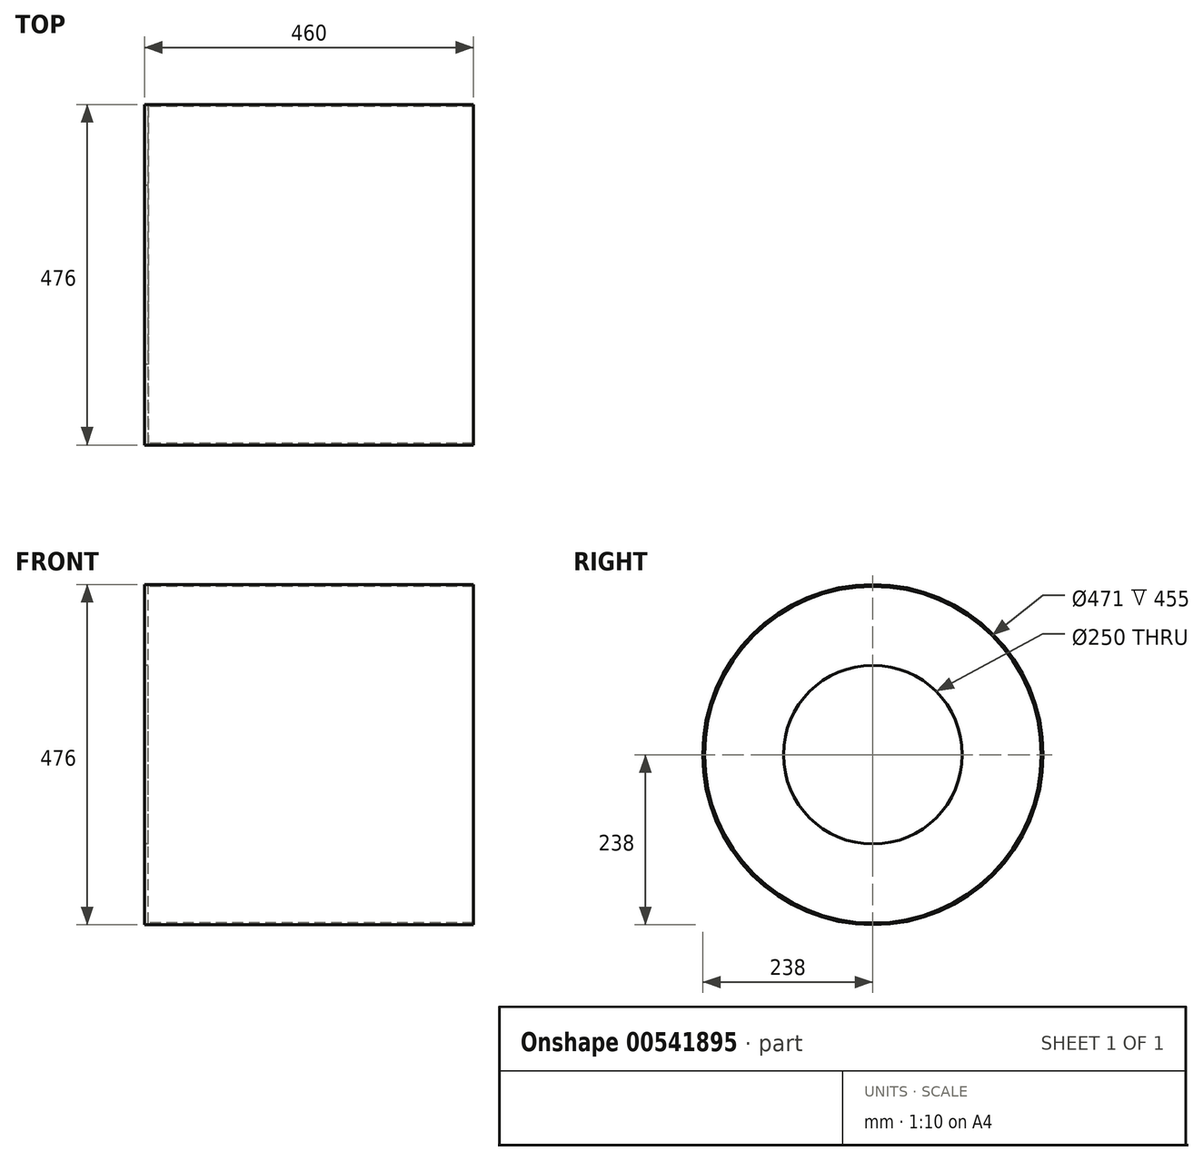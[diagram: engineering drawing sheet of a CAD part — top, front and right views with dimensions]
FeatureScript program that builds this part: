
annotation { "Feature Type Name" : "Feature", "Feature Type Description" : "" }
export const myFeature = defineFeature(function(context is Context, id is Id, definition is map)
    precondition{}
    {
        {
            var Q0;
            Q0=qCreatedBy(makeId("Right.planeOp"),FACE);
            var sketch = newSketch(context, id + "F0", { "sketchPlane" : qUnion([Q0])});
            skCircle(sketch, "E0", {"center": v(0, 0) * mm, "radius": 238 * mm});
            skCircle(sketch, "E1", {"center": v(0, 0) * mm, "radius": 235.5 * mm});
            skSolve(sketch);
        }
        {
            var Q0;
            Q0 = qSketchRegion(id + "F0", true);
            extrude(context, id + "F1", {"entities" : qUnion([Q0]), "depth" : 460 * mm, "offsetDistance" : 25 * mm});
        }
        {
            var Q0;
            Q0=qCreatedBy(makeId("Right.planeOp"),FACE);
            var sketch = newSketch(context, id + "F2", { "sketchPlane" : qUnion([Q0])});
            skCircle(sketch, "E2", {"center": v(0, 0) * mm, "radius": 238 * mm});
            skSolve(sketch);
        }
        {
            var Q0;
            Q0 = qSketchRegion(id + "F2", true);
            extrude(context, id + "F3", {"entities" : qUnion([Q0]), "operationType" : NewBodyOperationType.ADD, "depth" : 5 * mm, "offsetDistance" : 25 * mm});
        }
        {
            var Q0;
            Q0=makeQuery(id+"F3.boolean.opBoolean","MERGE",FACE,{"derivedFrom":[makeQuery(id+"F1.opExtrude","CAP_FACE",FACE,{"disambiguationData":[OSD([sQuery(id+"F0.wireOp",EDGE,"E0"),sQuery(id+"F0.wireOp",EDGE,"E1")])],"isStart":true}),makeQuery(id+"F3.opExtrude","CAP_FACE",FACE,{"disambiguationData":[OSD([sQuery(id+"F2.wireOp",EDGE,"E2")])],"isStart":true})]});
            var sketch = newSketch(context, id + "F4", { "sketchPlane" : qUnion([Q0])});
            skCircle(sketch, "E3", {"center": v(0, 0) * mm, "radius": 125 * mm});
            skSolve(sketch);
        }
        {
            var Q0;
            Q0=sQuery(id+"F4.wireOp",VERTEX,"E3.center");
            var Q1;
            Q1=makeQuery(id+"F1.opExtrude","SWEPT_BODY",BODY,{"disambiguationData":[OSD([sQuery(id+"F0.wireOp",EDGE,"E0"),sQuery(id+"F0.wireOp",EDGE,"E1")])]});
            hole(context, id + "F5", {"style" : HoleStyle.SIMPLE, "endStyle" : HoleEndStyle.BLIND, "holeDiameter" : 250 * mm, "holeDepth" : 430 * mm, "isTappedThrough" : true, "tappedDepth" : 12 * mm, "tapClearance" : 3, "locations" : qUnion([Q0]), "scope" : qUnion([Q1])});
        }
    });
